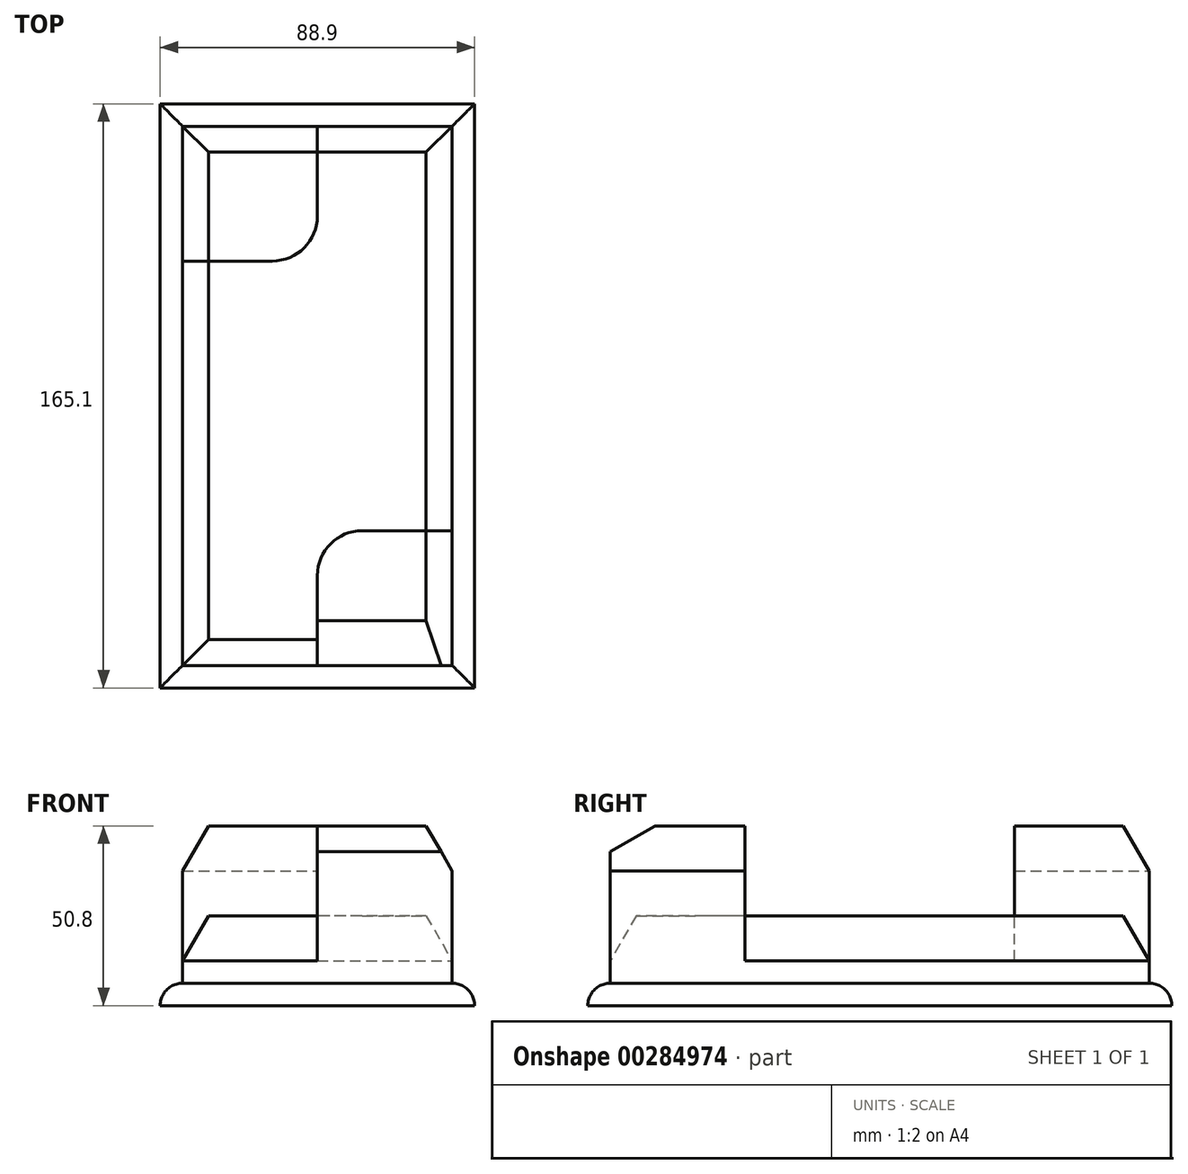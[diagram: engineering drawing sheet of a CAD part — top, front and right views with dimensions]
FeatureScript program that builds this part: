
annotation { "Feature Type Name" : "Feature", "Feature Type Description" : "" }
export const myFeature = defineFeature(function(context is Context, id is Id, definition is map)
    precondition{}
    {
        {
            var Q0;
            Q0=qCreatedBy(makeId("Top.planeOp"),FACE);
            var sketch = newSketch(context, id + "F0", { "sketchPlane" : qUnion([Q0])});
            skLineSegment(sketch, "E0.bottom", {"start": v(-56.11, 66.37) * mm, "end": v(32.79, 66.37) * mm});
            skLineSegment(sketch, "E0.top", {"start": v(-56.11, -98.73) * mm, "end": v(32.79, -98.73) * mm});
            skLineSegment(sketch, "E0.left", {"start": v(-56.11, 66.37) * mm, "end": v(-56.11, -98.73) * mm});
            skLineSegment(sketch, "E0.right", {"start": v(32.79, 66.37) * mm, "end": v(32.79, -98.73) * mm});
            skLineSegment(sketch, "E1.bottom", {"start": v(-49.76, 60.02) * mm, "end": v(26.44, 60.02) * mm});
            skLineSegment(sketch, "E1.top", {"start": v(-49.76, -92.38) * mm, "end": v(26.44, -92.38) * mm});
            skLineSegment(sketch, "E1.left", {"start": v(-49.76, 60.02) * mm, "end": v(-49.76, -92.38) * mm});
            skLineSegment(sketch, "E1.right", {"start": v(26.44, 60.02) * mm, "end": v(26.44, -92.38) * mm});
            skLineSegment(sketch, "E2", {"start": v(-11.66, 60.02) * mm, "end": v(-11.66, 34.62) * mm});
            skLineSegment(sketch, "E3", {"start": v(-24.36, 21.92) * mm, "end": v(-49.76, 21.92) * mm});
            skPoint(sketch, "E4.visualSharp", {"position": v(-11.66, 21.92) * mm});
            skArc(sketch, "E4.filletArc", {"start": v(-24.36, 21.92) * mm, "mid": v(-15.38, 25.64) * mm, "end": v(-11.66, 34.62) * mm});
            skLineSegment(sketch, "E5", {"start": v(-11.66, -92.38) * mm, "end": v(-11.66, -66.98) * mm});
            skLineSegment(sketch, "E6", {"start": v(1.04, -54.28) * mm, "end": v(26.44, -54.28) * mm});
            skPoint(sketch, "E7.visualSharp", {"position": v(-11.66, -54.28) * mm});
            skArc(sketch, "E7.filletArc", {"start": v(1.04, -54.28) * mm, "mid": v(-7.95, -58) * mm, "end": v(-11.66, -66.98) * mm});
            skSolve(sketch);
        }
        {
            var Q0;
            Q0=makeQuery(id+"F0.imprint","IMPRINT",FACE,{"disambiguationData":[TD([[makeQuery(id+"F0.imprint","IMPRINT",EDGE,{"derivedFrom":sQuery(id+"F0.wireOp",EDGE,"E0.bottom")}),-1.0]])]});
            extrude(context, id + "F1", {"entities" : qUnion([Q0]), "depth" : 6.35 * mm});
        }
        {
            var Q0;
            Q0=makeQuery(id+"F1.opExtrude","CAP_EDGE",EDGE,{"disambiguationData":[OSD([sQuery(id+"F0.wireOp",EDGE,"E0.right")])],"isStart":false});
            var Q1;
            Q1=makeQuery(id+"F1.opExtrude","CAP_EDGE",EDGE,{"disambiguationData":[OSD([sQuery(id+"F0.wireOp",EDGE,"E0.top")])],"isStart":false});
            var Q2;
            Q2=makeQuery(id+"F1.opExtrude","CAP_EDGE",EDGE,{"disambiguationData":[OSD([sQuery(id+"F0.wireOp",EDGE,"E0.left")])],"isStart":false});
            var Q3;
            Q3=makeQuery(id+"F1.opExtrude","CAP_EDGE",EDGE,{"disambiguationData":[OSD([sQuery(id+"F0.wireOp",EDGE,"E0.bottom")])],"isStart":false});
            fillet(context, id + "F2", {"entities" : qUnion([Q0, Q1, Q2, Q3]), "radius" : 6.35 * mm, "tangentPropagation" : true, "allowEdgeOverflow" : false});
        }
        {
            var Q0;
            {var subQ9=sQuery(id+"F0.wireOp",EDGE,"E2");Q0=makeQuery(id+"F0.imprint","IMPRINT",FACE,{"disambiguationData":[TD([[makeQuery(id+"F0.imprint","IMPRINT",EDGE,{"derivedFrom":subQ9}),1.0]])]});}
            extrude(context, id + "F3", {"entities" : qUnion([Q0]), "operationType" : NewBodyOperationType.ADD, "depth" : 25.4 * mm});
        }
        {
            var Q0;
            Q0=makeQuery(id+"F3.opExtrude","CAP_EDGE",EDGE,{"disambiguationData":[OSD([sQuery(id+"F0.wireOp",EDGE,"E1.bottom")])],"isStart":false});
            var Q1;
            Q1=makeQuery(id+"F3.opExtrude","CAP_EDGE",EDGE,{"disambiguationData":[OSD([sQuery(id+"F0.wireOp",EDGE,"E1.right")])],"isStart":false});
            var Q2;
            Q2=makeQuery(id+"F3.opExtrude","CAP_EDGE",EDGE,{"disambiguationData":[OSD([sQuery(id+"F0.wireOp",EDGE,"E1.top")])],"isStart":false});
            var Q3;
            Q3=makeQuery(id+"F3.opExtrude","CAP_EDGE",EDGE,{"disambiguationData":[OSD([sQuery(id+"F0.wireOp",EDGE,"E1.left")])],"isStart":false});
            chamfer(context, id + "F4", {"entities" : qUnion([Q0, Q1, Q2, Q3]), "chamferType" : ChamferType.OFFSET_ANGLE, "width" : 12.7 * mm, "oppositeDirection" : false, "angle" : 30 * degree, "tangentPropagation" : true});
        }
        {
            var Q0;
            {var subQ0=sQuery(id+"F0.wireOp",EDGE,"E2");Q0=makeQuery(id+"F0.imprint","IMPRINT",FACE,{"disambiguationData":[TD([[makeQuery(id+"F0.imprint","IMPRINT",EDGE,{"derivedFrom":subQ0}),-1.0]])]});}
            var Q1;
            {var subQ0=sQuery(id+"F0.wireOp",EDGE,"MRfEVyLt-ODYY-h9lc-bGD1-9heDdDpBYdyt");Q1=makeQuery(id+"F0.imprint","IMPRINT",FACE,{"disambiguationData":[TD([[makeQuery(id+"F0.imprint","IMPRINT",EDGE,{"derivedFrom":subQ0}),-1.0]])]});}
            var Q2;
            {var subQ0=sQuery(id+"F0.wireOp",EDGE,"E5");Q2=makeQuery(id+"F0.imprint","IMPRINT",FACE,{"disambiguationData":[TD([[makeQuery(id+"F0.imprint","IMPRINT",EDGE,{"derivedFrom":subQ0}),-1.0]])]});}
            extrude(context, id + "F5", {"entities" : qUnion([Q0, Q1, Q2]), "operationType" : NewBodyOperationType.ADD, "depth" : 50.8 * mm});
        }
        {
            var Q0;
            Q0=makeQuery(id+"F5.opExtrude","CAP_EDGE",EDGE,{"disambiguationData":[OSD([sQuery(id+"F0.wireOp",EDGE,"E1.bottom")])],"isStart":false});
            var Q1;
            Q1=makeQuery(id+"F5.opExtrude","CAP_EDGE",EDGE,{"disambiguationData":[OSD([sQuery(id+"F0.wireOp",EDGE,"E1.left")])],"isStart":false});
            var Q2;
            Q2=makeQuery(id+"F5.opExtrude","CAP_EDGE",EDGE,{"disambiguationData":[OSD([sQuery(id+"F0.wireOp",EDGE,"E1.right")])],"isStart":false});
            var Q3;
            Q3=makeQuery(id+"F5.opExtrude","CAP_EDGE",EDGE,{"disambiguationData":[OSD([sQuery(id+"F0.wireOp",EDGE,"E1.top")])],"isStart":false});
            chamfer(context, id + "F6", {"entities" : qUnion([Q0, Q1, Q2, Q3]), "chamferType" : ChamferType.OFFSET_ANGLE, "width" : 12.7 * mm, "oppositeDirection" : false, "angle" : 30 * degree, "tangentPropagation" : true});
        }
    });
